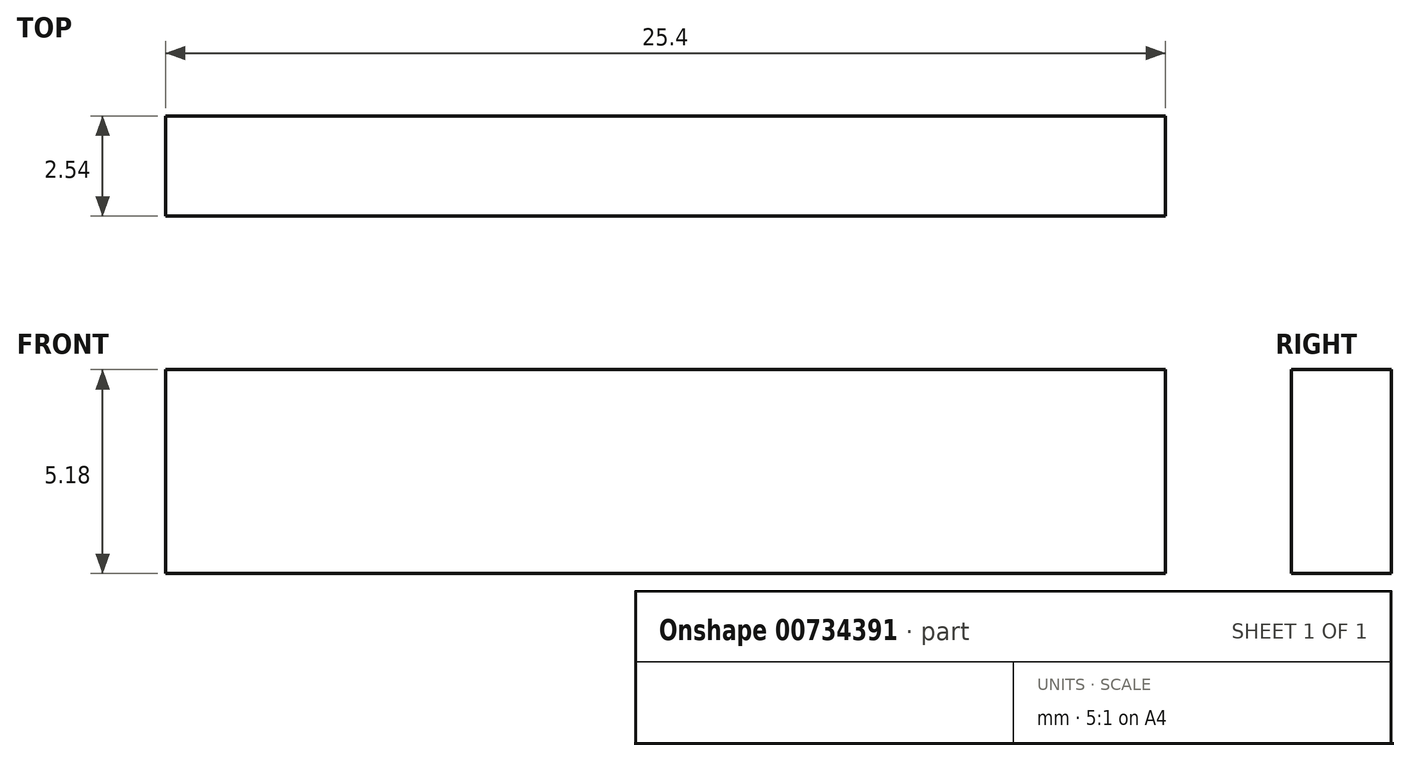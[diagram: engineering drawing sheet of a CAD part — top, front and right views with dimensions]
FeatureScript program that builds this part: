
annotation { "Feature Type Name" : "Feature", "Feature Type Description" : "" }
export const myFeature = defineFeature(function(context is Context, id is Id, definition is map)
    precondition{}
    {
        {
            var Q0;
            Q0=qCreatedBy(makeId("Front.planeOp"),FACE);
            var sketch = newSketch(context, id + "F0", { "sketchPlane" : qUnion([Q0])});
            skLineSegment(sketch, "E0", {"start": v(-24.5, 28.78) * mm, "end": v(0.9, 28.78) * mm});
            skLineSegment(sketch, "E1", {"start": v(-24.5, 28.78) * mm, "end": v(-24.5, 23.6) * mm});
            skLineSegment(sketch, "E2", {"start": v(-24.5, 23.6) * mm, "end": v(0.9, 23.6) * mm});
            skLineSegment(sketch, "E3", {"start": v(0.9, 23.6) * mm, "end": v(0.9, 28.78) * mm});
            skSolve(sketch);
        }
        {
            var Q0;
            Q0 = qSketchRegion(id + "F0", true);
            extrude(context, id + "F1", {"entities" : qUnion([Q0]), "depth" : 2.54 * mm, "offsetDistance" : 25.4 * mm});
        }
    });
